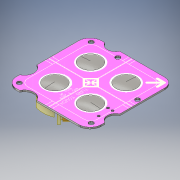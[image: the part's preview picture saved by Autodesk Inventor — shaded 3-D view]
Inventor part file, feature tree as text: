
AUTODESK INVENTOR PART (.ipt)
format: ipt  version: 2016 (Build 200138000, 138)  size: 1,544,704 bytes
history: native  units: in
note: dims shown in document units (in); Inventor stores cm internally (conversion verified against a paired STEP export)
features: other x9, sketch x4, plane x2, extrude x1, loft x1, pattern_circular x1, move_body x1, projected_geometry x1
ambient origin geometry x8: Origin, YZ Plane, XZ Plane, XY Plane, X Axis, Y Axis, Z Axis, Center Point
bodies: Solid1 (feature_tree), Solid6 (feature_tree), Solid7 (feature_tree), Solid8 (feature_tree), Solid9 (feature_tree)
feature tree (20):
  plane  "Work Plane3"
  extrude  "PCB Extrusion"  Depth=0.35in
  other  "PCB Mating Holes"
  other  "Decal3"
  other  "Decal4"
  sketch  "Sketch10"  dims[d55=0.014in d56=0.0in d57=90.0deg]
  plane  "Work Plane2"
  loft  "Loft2"
  pattern_circular  "Circular Pattern2"  Count=4 Angle=360.0deg
  other  "NONE:1"
  other  "NONE_1:1"
  other  "NONE_2:1"
  move_body  "Move Body4"
  other  "PCB Sketch"
  sketch  "Sketch8"  dims[d1=0.028in d2=0.0in]
  other  "Image3"
  sketch  "Sketch9"  dims[d44=1.0in d45=0.028in d46=0.0in d47=-1.0in d48=0.0in d49=-0.188in d50=135.0deg d51=1.02in d52=0.0in d53=0.23in d54=0.35in]
  other  "Image4"
  sketch  "Sketch11"  dims[d58=0.3937in d59=90.0deg d60=1.5748in d61=360.0deg d75=1.45in d87=-0.0in d95=180.0deg d96=90.0deg]
  projected_geometry  "Projected Loop1"
